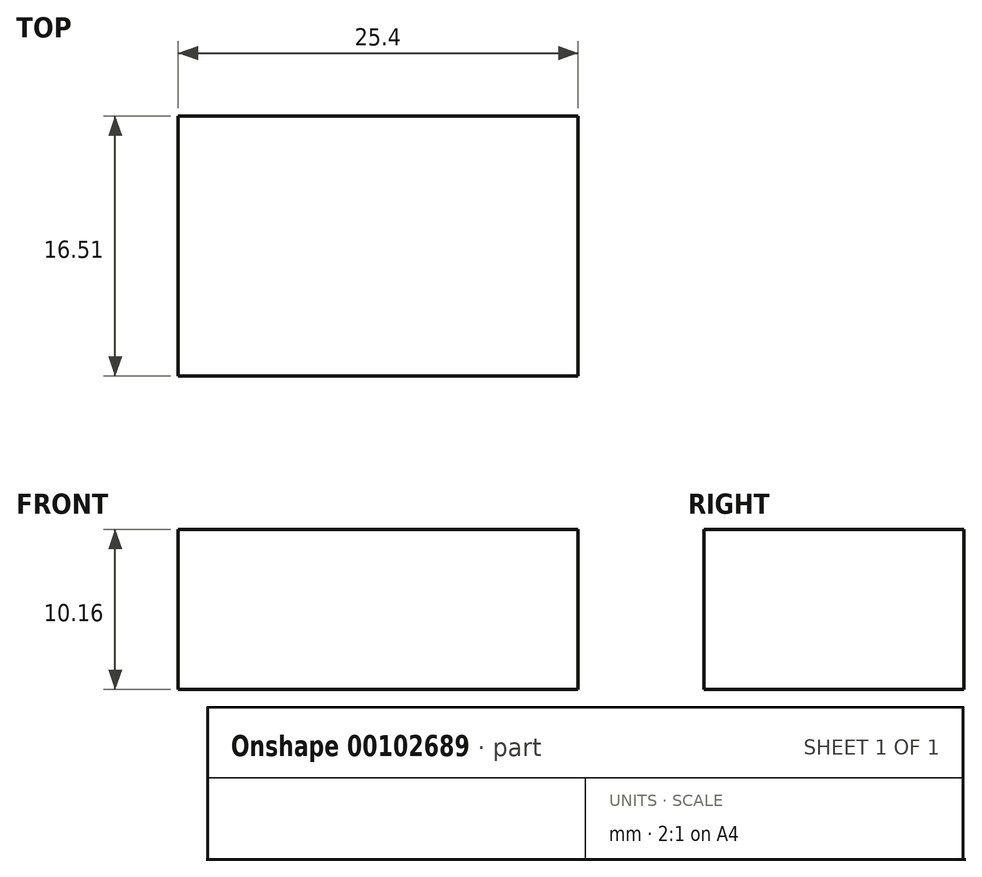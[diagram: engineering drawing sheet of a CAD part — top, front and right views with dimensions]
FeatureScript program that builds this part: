
annotation { "Feature Type Name" : "Feature", "Feature Type Description" : "" }
export const myFeature = defineFeature(function(context is Context, id is Id, definition is map)
    precondition{}
    {
        {
            var Q0;
            Q0=qCreatedBy(makeId("Top.planeOp"),FACE);
            var sketch = newSketch(context, id + "F0", { "sketchPlane" : qUnion([Q0])});
            skLineSegment(sketch, "E0.bottom", {"start": v(-4.46, 14.7) * mm, "end": v(46.34, 14.7) * mm});
            skLineSegment(sketch, "E0.top", {"start": v(-4.46, -1.81) * mm, "end": v(46.34, -1.81) * mm});
            skLineSegment(sketch, "E0.left", {"start": v(-4.46, 14.7) * mm, "end": v(-4.46, -1.81) * mm});
            skLineSegment(sketch, "E0.right", {"start": v(46.34, 14.7) * mm, "end": v(46.34, -1.81) * mm});
            skSolve(sketch);
        }
        {
            var Q0;
            Q0=makeQuery(id+"F0.imprint","IMPRINT",FACE,{"disambiguationData":[TD([[makeQuery(id+"F0.imprint","IMPRINT",EDGE,{"derivedFrom":sQuery(id+"F0.wireOp",EDGE,"E0.bottom")}),-1.0]])]});
            extrude(context, id + "F1", {"entities" : qUnion([Q0]), "depth" : 10.16 * mm});
        }
        {
            var Q0;
            Q0=makeQuery(id+"F1.opExtrude","CAP_FACE",FACE,{"disambiguationData":[OSD([sQuery(id+"F0.wireOp",EDGE,"E0.bottom"),sQuery(id+"F0.wireOp",EDGE,"E0.top"),sQuery(id+"F0.wireOp",EDGE,"E0.left"),sQuery(id+"F0.wireOp",EDGE,"E0.right")])],"isStart":true});
            var sketch = newSketch(context, id + "F2", { "sketchPlane" : qUnion([Q0])});
            skLineSegment(sketch, "E1", {"start": v(-4.46, -6.44) * mm, "end": v(46.34, -6.44) * mm});
            skLineSegment(sketch, "E2", {"start": v(20.94, 1.81) * mm, "end": v(20.94, -14.7) * mm});
            skCircle(sketch, "E3", {"center": v(20.94, -6.44) * mm, "radius": 3.81 * mm});
            skSolve(sketch);
        }
        {
            var Q0;
            {var subQ0=sQuery(id+"F2.wireOp",EDGE,"E3");var subQ1=sQuery(id+"F2.wireOp",EDGE,"E1");var subQ2=makeQuery(id+"F2.imprint","INTERSECT",VERTEX,{"disambiguationData":[OD(0.0)],"derivedFrom":[subQ1,subQ0]});Q0=makeQuery(id+"F2.imprint","IMPRINT",FACE,{"disambiguationData":[TD([[makeQuery(id+"F2.imprint","IMPRINT",EDGE,{"disambiguationData":[TD([[subQ2,-1.0]])],"derivedFrom":subQ1}),1.0]])]});}
            var Q1;
            {var subQ0=sQuery(id+"F2.wireOp",EDGE,"E2");var subQ1=sQuery(id+"F2.wireOp",EDGE,"E1");var subQ2=makeQuery(id+"F2.imprint","INTERSECT",VERTEX,{"derivedFrom":[subQ1,subQ0]});Q1=makeQuery(id+"F2.imprint","IMPRINT",FACE,{"disambiguationData":[TD([[makeQuery(id+"F2.imprint","IMPRINT",EDGE,{"disambiguationData":[TD([[subQ2,-1.0]])],"derivedFrom":subQ1}),1.0]])]});}
            var Q2;
            {var subQ0=sQuery(id+"F2.wireOp",EDGE,"E3");var subQ1=sQuery(id+"F2.wireOp",EDGE,"E1");var subQ2=makeQuery(id+"F2.imprint","INTERSECT",VERTEX,{"disambiguationData":[OD(0.0)],"derivedFrom":[subQ1,subQ0]});Q2=makeQuery(id+"F2.imprint","IMPRINT",FACE,{"disambiguationData":[TD([[makeQuery(id+"F2.imprint","IMPRINT",EDGE,{"disambiguationData":[TD([[subQ2,-1.0]])],"derivedFrom":subQ1}),-1.0]])]});}
            var Q3;
            {var subQ0=sQuery(id+"F2.wireOp",EDGE,"E2");var subQ1=sQuery(id+"F2.wireOp",EDGE,"E1");var subQ2=makeQuery(id+"F2.imprint","INTERSECT",VERTEX,{"derivedFrom":[subQ1,subQ0]});Q3=makeQuery(id+"F2.imprint","IMPRINT",FACE,{"disambiguationData":[TD([[makeQuery(id+"F2.imprint","IMPRINT",EDGE,{"disambiguationData":[TD([[subQ2,-1.0]])],"derivedFrom":subQ1}),-1.0]])]});}
            extrude(context, id + "F3", {"entities" : qUnion([Q0, Q1, Q2, Q3]), "operationType" : NewBodyOperationType.REMOVE, "oppositeDirection" : true, "depth" : 25.4 * mm});
        }
    });
